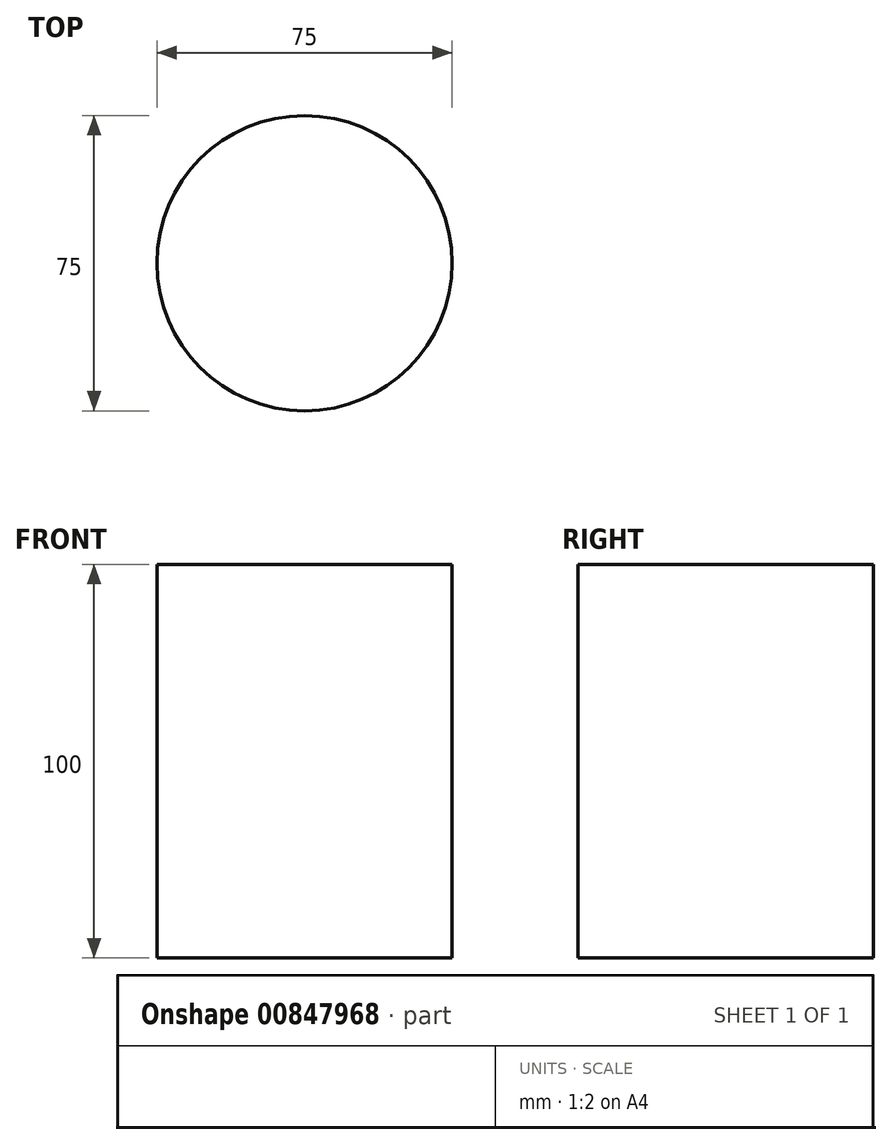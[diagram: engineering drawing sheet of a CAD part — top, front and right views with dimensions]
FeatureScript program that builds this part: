
annotation { "Feature Type Name" : "Feature", "Feature Type Description" : "" }
export const myFeature = defineFeature(function(context is Context, id is Id, definition is map)
    precondition{}
    {
        {
            var Q0;
            Q0=qCreatedBy(makeId("Top.planeOp"),FACE);
            var sketch = newSketch(context, id + "F0", { "sketchPlane" : qUnion([Q0])});
            skCircle(sketch, "E0", {"center": v(0, 0) * mm, "radius": 37.5 * mm});
            skSolve(sketch);
        }
        {
            var Q0;
            Q0 = qSketchRegion(id + "F0", true);
            extrude(context, id + "F1", {"entities" : qUnion([Q0]), "depth" : 100 * mm, "offsetDistance" : 25 * mm});
        }
    });
